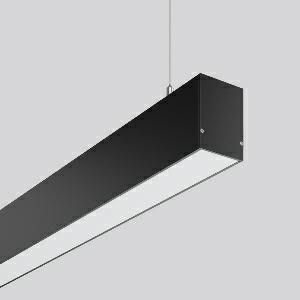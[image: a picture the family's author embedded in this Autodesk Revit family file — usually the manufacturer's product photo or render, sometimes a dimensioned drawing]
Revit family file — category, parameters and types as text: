
# Revit family: less_is_more_50_312315_003_1_fa31
name_source: partatom
category: Lighting Fixtures
units: mm (PartAtom-declared; Revit-internal decimal feet)

## family parameters
Cut with Voids When Loaded = No
Host = Face
Light Source = No
Part Type = Normal
Room Calculation Point = No
Round Connector Dimension = Use Diameter
Shared = No

## types (1)
- LESS IS MORE 50 (1 x LED Modul 840, 5650 lm, 4000)
    Apparent Load = 47 VA
    CIE Flux Codes = 48 79 95 100 100
    Color Rendering = 80
    Color Temperature = 4000
    Default Elevation = 1800 mm
    Description = Series: LESS IS MORE 50
Linear pendant luminaire for aesthetically sophisticated lighting. Housing: extruded aluminium profile, powder-coated. End cap aluminium powder-coated. Canopy made of aluminium, powder-coated. Diffuser made of non-yellowing plastic (PMMA), opal. Direct light emission. Suitable for pendant. 2-point steel cable suspension freely positionable and infinitely height-adjustable. Special lengths available on request. LED unit with integrated converter interchangeable and removable. Suitable for through-wiring. With sensors or as a safety luminaire on request. 
Colour: deep black, matt (RAL 9005)
Length: 1967 mm
Width: 57 mm
Height: 75 mm
Suspension length: 2000 mm
Lamp: LED
Socket: without socket
Colour temperature: 4000K
Colour rendering index (CRI): 80
System power: 47 W
Rated luminous flux: 5650 lm
Luminous efficiency: 120 lm/W
Control gear: Regulated power supply
Protection class: I
Type of protection: IP 20
    Height = 75 mm
    Lamp = 1 x LED Modul 840
    Lamp Light Flux = 5650 lm
    Lamp count = 1
    Length = 1967 mm
    Lifetime = 50000 h
    Luminous efficacy = 120 lm/W
    Manufacturer = RZB
    ModVariant = No
    Model = 312315.003.1
    Mounting Place = Ceiling
    Mounting Type = Pendant
    Number of Poles = 1
    OnlyDefault = Yes
    Power Factor = 1
    Product Name = LESS IS MORE 50
    Product group = Pendant LED linear luminaires
    ProductGroupID = 907
    Protection Class = Protection class I
    Protection Degree = IP 20
    RLX_Detail_Level = 1
    RLX_Emergency_Light_Flux = 0 lm
    RLX_Emergency_Type = 0
    RLX_Emergency_Type_DB = No
    RlxData = <blob elided: 28857 chars, md5=9c706629>
    Socket = socket
    Standby Power = 0 W
    System Light Flux = 5650 lm
    System Power = 47 W
    Type Comments = Product without accessories
    Type Image = 312318.003.jpg
    URL = http://relux.com
    VarID = ---
    Voltage = 230 V
    Voltage Range = 220-240 V
    Weight = 0.00 kg
    Width = 57 mm

## geometry (parser evidence)
native form markers: Blend x4, Sweep x9
no freeform markers — native parametric forms only
